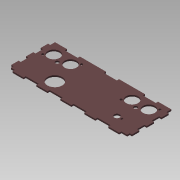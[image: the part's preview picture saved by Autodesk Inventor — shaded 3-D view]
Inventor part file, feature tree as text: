
AUTODESK INVENTOR PART (.ipt)
format: ipt  version: 2015 SP1 (Build 190203100, 203)  size: 190,976 bytes
history: native  units: mm
features: extrude x1, sketch x1
ambient origin geometry x8: Origin, YZ Plane, XZ Plane, XY Plane, X Axis, Y Axis, Z Axis, Center Point
bodies: Solid1 (feature_tree)
feature tree (2):
  extrude  "Extrusion1"  Depth=15.0mm
  sketch  "Sketch1"  dims[d2=20.0mm d4=15.0mm d5=3.0mm d8=30.0mm d10=32.5mm d11=30.0mm d13=32.5mm d16=1.5mm d17=3.0mm d18=10.0mm d19=20.0mm d21=20.0mm d22=20.0mm d24=20.0mm d27=2.0mm d28=0.0mm]
